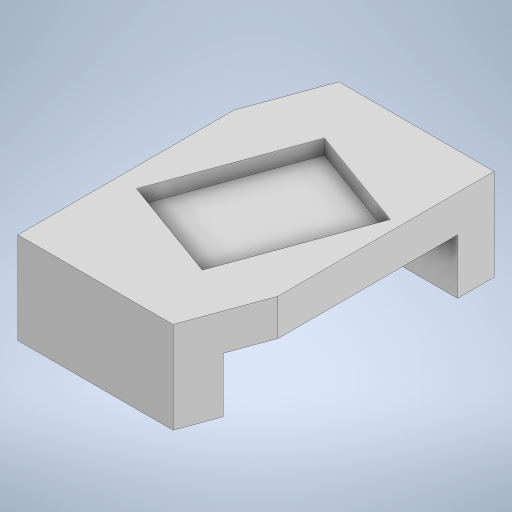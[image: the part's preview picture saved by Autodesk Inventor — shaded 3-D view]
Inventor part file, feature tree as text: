
AUTODESK INVENTOR PART (.ipt)
format: ipt  version: 2023.2 (Build 272271030, 271C)  size: 247,808 bytes
history: native  units: mm
features: extrude x3, sketch x3, projected_geometry x3, plane x2
ambient origin geometry x8: Origin, YZ Plane, XZ Plane, XY Plane, X Axis, Y Axis, Z Axis, Center Point
bodies: Solid1 (feature_tree)
feature tree (11):
  extrude  "Extrusion1"  Depth=80.0mm
  plane  "Work Plane1"
  extrude  "Extrusion2"  Depth=21.0mm
  plane  "Work Plane2"
  extrude  "Extrusion3"  Depth=21.0mm
  sketch  "Sketch1"  dims[d0=50.0mm d1=80.0mm]
  sketch  "Sketch2"  dims[d2=21.0mm d3=3.490659mm]
  projected_geometry  "Projected Loop1"
  projected_geometry  "Projected Loop2"
  sketch  "Sketch3"  dims[d4=3.490659mm d5=21.0mm d6=25.0mm d7=0.0mm d8=25.25mm d9=60.0mm d10=10.0mm d11=15.0mm d12=0.0mm d13=0.0mm d14=25.0mm d15=30.0mm d16=40.0mm d17=30.0mm d18=25.0mm d19=12.217305mm d20=5.3mm d21=4.0mm d22=0.0mm]
  projected_geometry  "Projected Loop3"
